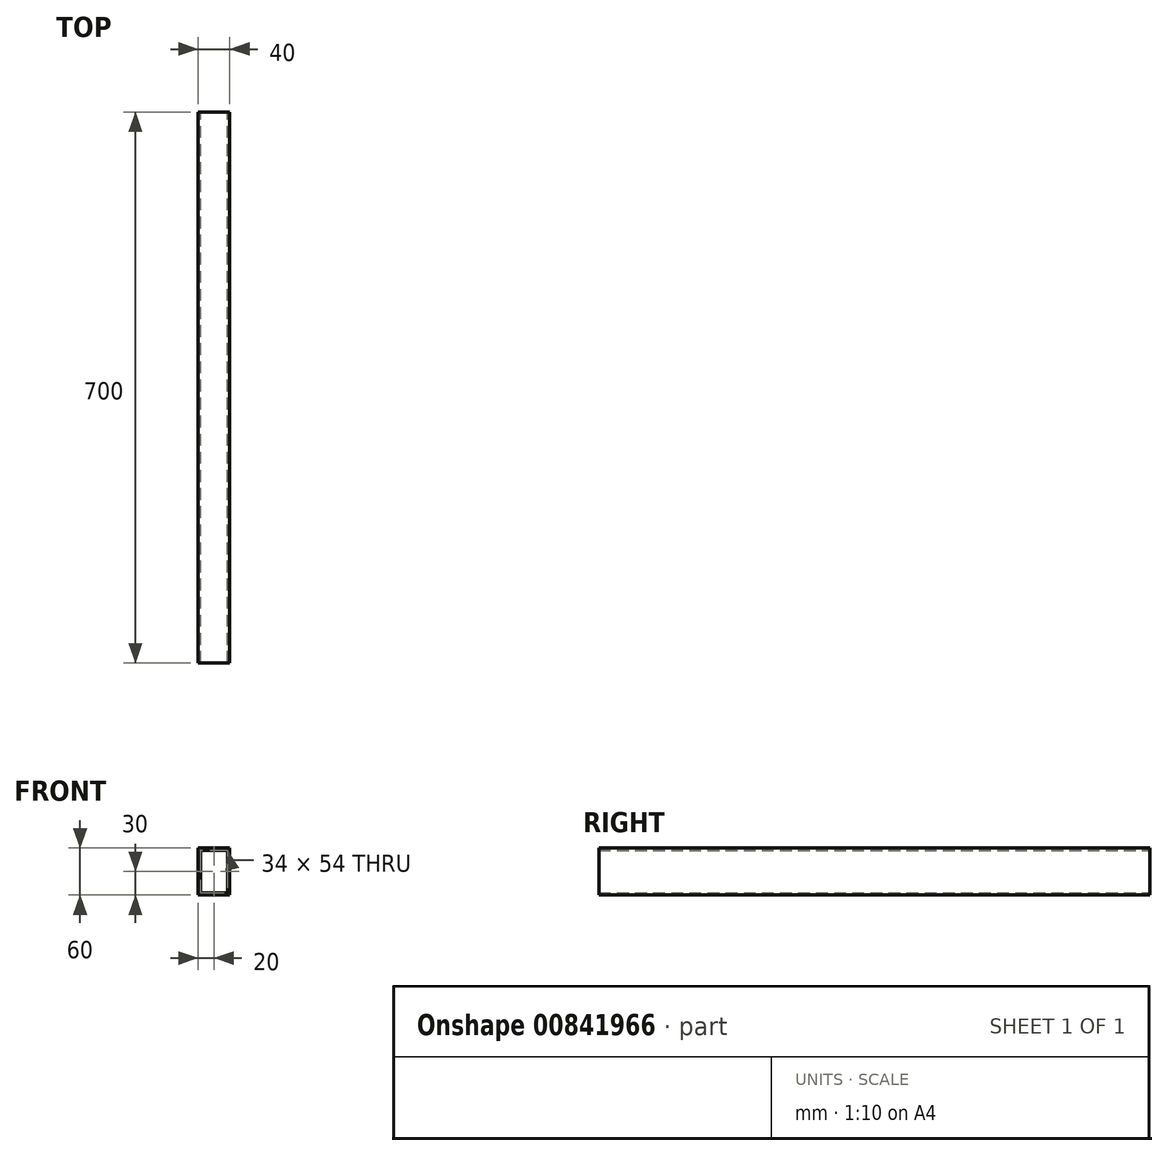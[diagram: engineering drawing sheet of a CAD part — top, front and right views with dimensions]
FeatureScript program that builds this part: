
annotation { "Feature Type Name" : "Feature", "Feature Type Description" : "" }
export const myFeature = defineFeature(function(context is Context, id is Id, definition is map)
    precondition{}
    {
        {
            var Q0;
            Q0=qCreatedBy(makeId("Front.planeOp"),FACE);
            var sketch = newSketch(context, id + "F0", { "sketchPlane" : qUnion([Q0])});
            skLineSegment(sketch, "E0.bottom", {"start": v(-20, 30) * mm, "end": v(20, 30) * mm});
            skLineSegment(sketch, "E0.top", {"start": v(-20, -30) * mm, "end": v(20, -30) * mm});
            skLineSegment(sketch, "E0.left", {"start": v(-20, 30) * mm, "end": v(-20, -30) * mm});
            skLineSegment(sketch, "E0.right", {"start": v(20, 30) * mm, "end": v(20, -30) * mm});
            skLineSegment(sketch, "E1.0", {"start": v(-17, 27) * mm, "end": v(-17, -27) * mm});
            skLineSegment(sketch, "E1.1", {"start": v(-17, 27) * mm, "end": v(17, 27) * mm});
            skLineSegment(sketch, "E1.2", {"start": v(17, 27) * mm, "end": v(17, -27) * mm});
            skLineSegment(sketch, "E1.3", {"start": v(-17, -27) * mm, "end": v(17, -27) * mm});
            skSolve(sketch);
        }
        {
            var Q0;
            Q0=makeQuery(id+"F0.imprint","IMPRINT",FACE,{"disambiguationData":[TD([[makeQuery(id+"F0.imprint","IMPRINT",EDGE,{"derivedFrom":sQuery(id+"F0.wireOp",EDGE,"E0.bottom")}),-1.0]])]});
            extrude(context, id + "F1", {"entities" : qUnion([Q0]), "endBound" : BoundingType.SYMMETRIC, "depth" : 700 * mm, "offsetDistance" : 25 * mm});
        }
    });
